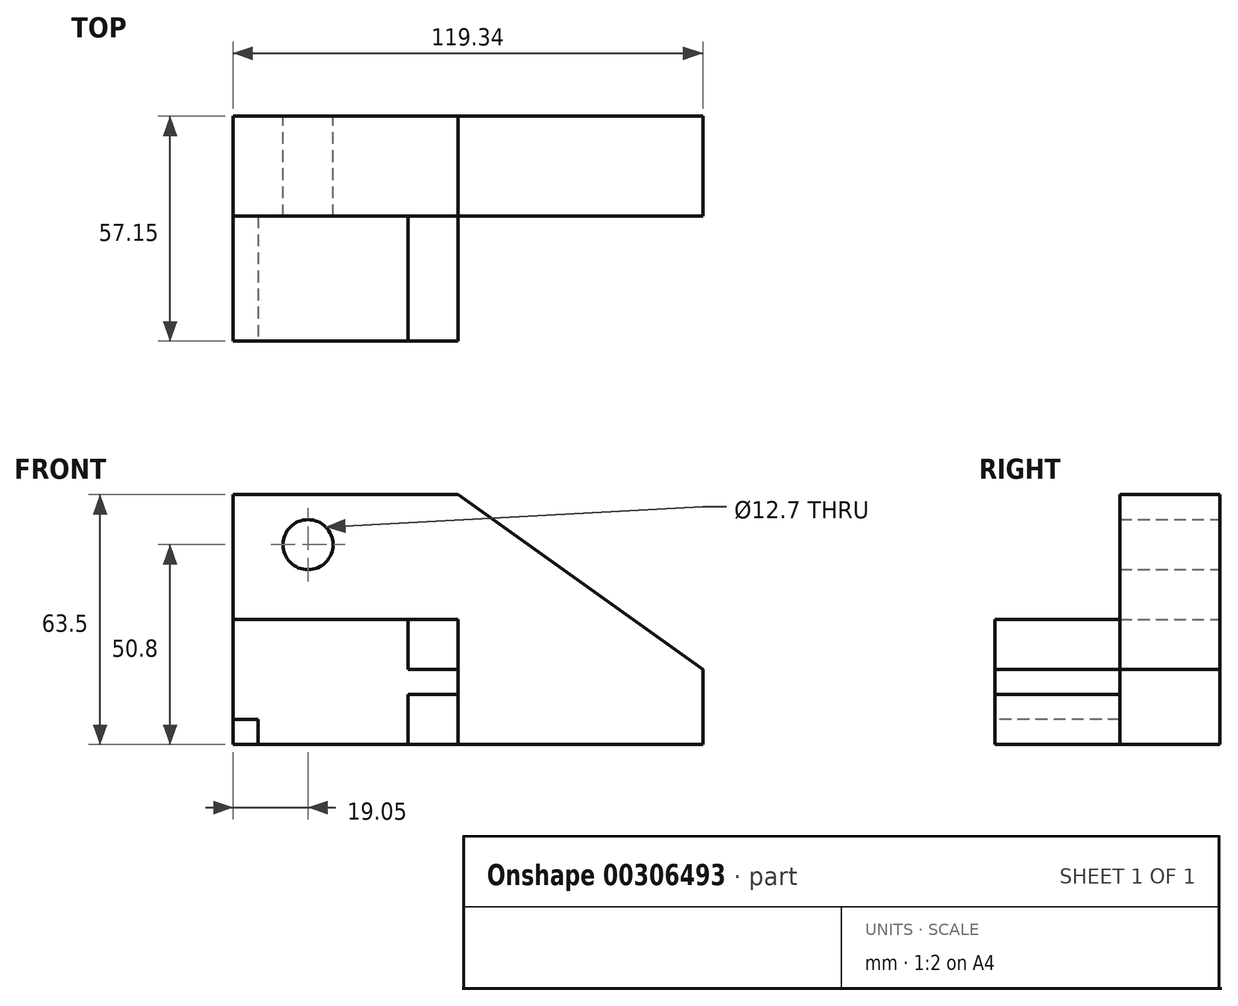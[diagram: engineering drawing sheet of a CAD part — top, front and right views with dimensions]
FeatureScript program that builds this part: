
annotation { "Feature Type Name" : "Feature", "Feature Type Description" : "" }
export const myFeature = defineFeature(function(context is Context, id is Id, definition is map)
    precondition{}
    {
        {
            var Q0;
            Q0=qCreatedBy(makeId("Front.planeOp"),FACE);
            var sketch = newSketch(context, id + "F0", { "sketchPlane" : qUnion([Q0])});
            skLineSegment(sketch, "E0", {"start": v(-57.15, 31.75) * mm, "end": v(-57.15, 0) * mm});
            skLineSegment(sketch, "E1", {"start": v(-57.15, 0) * mm, "end": v(0, 0) * mm});
            skLineSegment(sketch, "E2", {"start": v(-57.15, 31.75) * mm, "end": v(0, 31.75) * mm});
            skLineSegment(sketch, "E3", {"start": v(0, 31.75) * mm, "end": v(0, 0) * mm});
            skLineSegment(sketch, "E4", {"start": v(-57.15, 31.75) * mm, "end": v(-57.15, 63.5) * mm});
            skLineSegment(sketch, "E5", {"start": v(-57.15, 63.5) * mm, "end": v(0, 63.5) * mm});
            skLineSegment(sketch, "E6", {"start": v(0, 63.5) * mm, "end": v(62.19, 19.05) * mm});
            skLineSegment(sketch, "E7", {"start": v(62.19, 19.05) * mm, "end": v(62.19, 0) * mm});
            skLineSegment(sketch, "E8", {"start": v(0, 0) * mm, "end": v(62.19, 0) * mm});
            skCircle(sketch, "E9", {"center": v(-38.1, 50.8) * mm, "radius": 6.35 * mm});
            skSolve(sketch);
        }
        {
            var Q0;
            Q0=makeQuery(id+"F0.imprint","IMPRINT",FACE,{"disambiguationData":[TD([[makeQuery(id+"F0.imprint","IMPRINT",EDGE,{"derivedFrom":sQuery(id+"F0.wireOp",EDGE,"E2")}),1.0]])]});
            extrude(context, id + "F1", {"entities" : qUnion([Q0]), "depth" : 25.4 * mm});
        }
        {
            var Q0;
            Q0=makeQuery(id+"F0.imprint","IMPRINT",FACE,{"disambiguationData":[TD([[makeQuery(id+"F0.imprint","IMPRINT",EDGE,{"derivedFrom":sQuery(id+"F0.wireOp",EDGE,"E0")}),1.0]])]});
            extrude(context, id + "F2", {"entities" : qUnion([Q0]), "depth" : 57.15 * mm});
        }
        {
            var Q0;
            Q0=makeQuery(id+"F2.opExtrude","CAP_FACE",FACE,{"disambiguationData":[OSD([sQuery(id+"F0.wireOp",EDGE,"E0"),sQuery(id+"F0.wireOp",EDGE,"E1"),sQuery(id+"F0.wireOp",EDGE,"E2"),sQuery(id+"F0.wireOp",EDGE,"E3")])],"isStart":false});
            var sketch = newSketch(context, id + "F3", { "sketchPlane" : qUnion([Q0])});
            skLineSegment(sketch, "E10", {"start": v(-57.15, 6.35) * mm, "end": v(-50.8, 6.35) * mm});
            skLineSegment(sketch, "E11", {"start": v(-50.8, 6.35) * mm, "end": v(-50.8, 0) * mm});
            skLineSegment(sketch, "E12", {"start": v(-50.8, 0) * mm, "end": v(-57.15, 0) * mm});
            skLineSegment(sketch, "E13", {"start": v(-57.15, 0) * mm, "end": v(-57.15, 6.35) * mm});
            skLineSegment(sketch, "E14", {"start": v(-12.7, 31.75) * mm, "end": v(-12.7, 19.05) * mm});
            skLineSegment(sketch, "E15", {"start": v(-12.7, 19.05) * mm, "end": v(0, 19.05) * mm});
            skLineSegment(sketch, "E16", {"start": v(-12.7, 31.75) * mm, "end": v(0, 31.75) * mm});
            skLineSegment(sketch, "E17", {"start": v(0, 31.75) * mm, "end": v(0, 19.05) * mm});
            skLineSegment(sketch, "E18", {"start": v(0, 12.7) * mm, "end": v(-12.7, 12.7) * mm});
            skLineSegment(sketch, "E19", {"start": v(-12.7, 12.7) * mm, "end": v(-12.7, 0) * mm});
            skLineSegment(sketch, "E20", {"start": v(-12.7, 0) * mm, "end": v(0, 0) * mm});
            skLineSegment(sketch, "E21", {"start": v(0, 0) * mm, "end": v(0, 12.7) * mm});
            skSolve(sketch);
        }
        {
            var Q0;
            Q0 = qSketchRegion(id + "F3", true);
            extrude(context, id + "F4", {"entities" : qUnion([Q0]), "operationType" : NewBodyOperationType.REMOVE, "oppositeDirection" : true, "depth" : 31.75 * mm});
        }
    });
